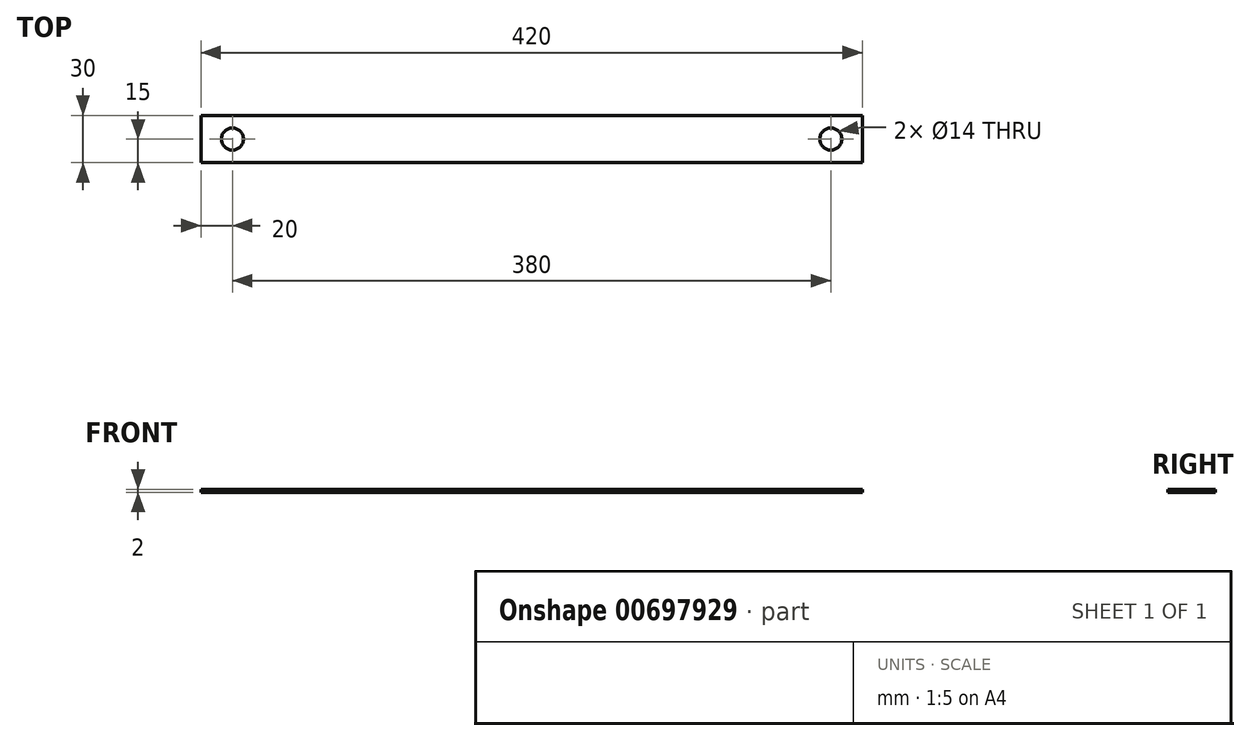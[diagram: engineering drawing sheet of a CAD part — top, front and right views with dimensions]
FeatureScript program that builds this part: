
annotation { "Feature Type Name" : "Feature", "Feature Type Description" : "" }
export const myFeature = defineFeature(function(context is Context, id is Id, definition is map)
    precondition{}
    {
        {
            var Q0;
            Q0=qCreatedBy(makeId("Top.planeOp"),FACE);
            var sketch = newSketch(context, id + "F0", { "sketchPlane" : qUnion([Q0])});
            skLineSegment(sketch, "E0.bottom", {"start": v(210, -15) * mm, "end": v(-210, -15) * mm});
            skLineSegment(sketch, "E0.top", {"start": v(210, 15) * mm, "end": v(-210, 15) * mm});
            skLineSegment(sketch, "E0.left", {"start": v(210, -15) * mm, "end": v(210, 15) * mm});
            skLineSegment(sketch, "E0.right", {"start": v(-210, -15) * mm, "end": v(-210, 15) * mm});
            skPoint(sketch, "E0.middle", {"position": v(0, 0) * mm});
            skSolve(sketch);
        }
        {
            var Q0;
            Q0=makeQuery(id+"F0.imprint","IMPRINT",FACE,{"disambiguationData":[TD([[makeQuery(id+"F0.imprint","IMPRINT",EDGE,{"derivedFrom":sQuery(id+"F0.wireOp",EDGE,"E0.bottom")}),-1.0]])]});
            var sketch = newSketch(context, id + "F1", { "sketchPlane" : qUnion([Q0])});
            skCircle(sketch, "E1", {"center": v(-190, 0) * mm, "radius": 7 * mm});
            skCircle(sketch, "E2", {"center": v(190, 0) * mm, "radius": 7 * mm});
            skSolve(sketch);
        }
        {
            var Q0;
            Q0=makeQuery(id+"F1.imprint","IMPRINT",FACE,{"disambiguationData":[TD([[makeQuery(id+"F1.imprint","IMPRINT",EDGE,{"derivedFrom":sQuery(id+"F1.wireOp",EDGE,"E1")}),-1.0]])]});
            extrude(context, id + "F2", {"entities" : qUnion([Q0]), "endBound" : BoundingType.SYMMETRIC, "depth" : 2 * mm, "offsetDistance" : 25 * mm});
        }
    });
